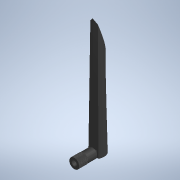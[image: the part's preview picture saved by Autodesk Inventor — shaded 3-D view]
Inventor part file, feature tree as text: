
AUTODESK INVENTOR PART (.ipt)
format: ipt  version: 2022 (Build 260153000, 153)  size: 239,616 bytes
history: native  units: mm (DEFAULTED — no unit token found)
features: other x8, sketch x2, extrude x1, pattern_circular x1
bodies: Body1 (feature_tree)
feature tree (12):
  other  "Sólido1"
  other  "Origen"
  sketch  "Boceto1"  dims[d0=135.495mm d1=0.0mm]
  extrude  "Extrusión1"  [1 undecoded]
  other  "Plano YZ"
  other  "Plano XZ"
  other  "Plano XY"
  other  "Eje X"
  other  "Eje Y"
  other  "Eje Z"
  sketch  "Boceto2"
  pattern_circular  "CirPattern1"
note: 1 required parameter value undecoded (feature->parameter linkage not recoverable at this tier; creation-order binding heuristic only, values carry confidence <= 0.55)
